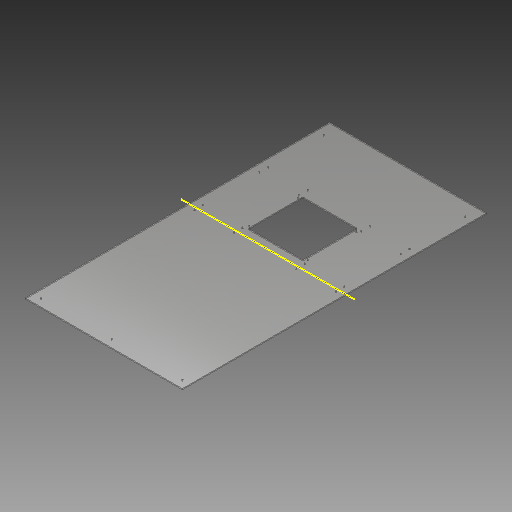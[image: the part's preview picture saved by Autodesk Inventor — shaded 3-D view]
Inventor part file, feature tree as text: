
AUTODESK INVENTOR PART (.ipt)
format: ipt  version: 2018 (Build 220112000, 112)  size: 150,016 bytes
history: native  units: in
note: dims shown in document units (in); Inventor stores cm internally (conversion verified against a paired STEP export)
features: plane x1, split x1, imported_body x1
ambient origin geometry x8: Origin, YZ Plane, XZ Plane, XY Plane, X Axis, Y Axis, Z Axis, Center Point
bodies: Solid1 (feature_tree), Solid2 (feature_tree), Solid3 (feature_tree)
feature tree (3):
  plane  "Work Plane1"
  split  "Split1"
  imported_body  "Imported1"
